# Revit family: Bath-Freestanding-KOHLER-Stillness-K-EX31414T_1
name_source: partatom
category: Plumbing Fixtures
units: mm (PartAtom-declared; Revit-internal decimal feet)

## family parameters
Cut with Voids When Loaded = No
Host = Face
Maintain Annotation Orientation = No
OmniClass Number = 23.31.15.00
OmniClass Title = Bathtubs
Part Type = Normal
Room Calculation Point = No
Round Connector Dimension = Use Diameter
Shared = No

## types (1)
- HW1-Honed White
    ADA Compliant = No
    Assembly Code = D2010500
    CW Connection = No
    Cold Water Inlet = Cold Water Inlet
    Date Modified = 04/27/2022
    Default Elevation = 0"
    Description = INFINITY FREESTANDING BATH (EXQ)
    Drain Included = Yes
    Finish = KOHLER-Acrylic-HW1-Honed_White
    HW Connection = No
    Height = 29 5/8"
    Hot Water Inlet = Hot Water Inlet
    Length = 46"
    Manufacturer = Kohler Co.
    Master Format 2014 = 22 41 19
    Master Format 2014 Name = Residential Bathtubs
    Material = Acrylic
    Model = K-EX31414T-HW1
    Product Name = Stillness
    Secondary Finish = KOHLER-Acrylic-0-White
    Type = 1
    URL = http://www.kohler.com.cn
    Vent Connection = No
    Waste Connection = Yes
    Waste Water Outlet = Waste Water Outlet
    WaterSense Certified = No
    Width = 46"

## geometry (parser evidence)
native form markers: Sweep x6
no freeform markers — native parametric forms only
